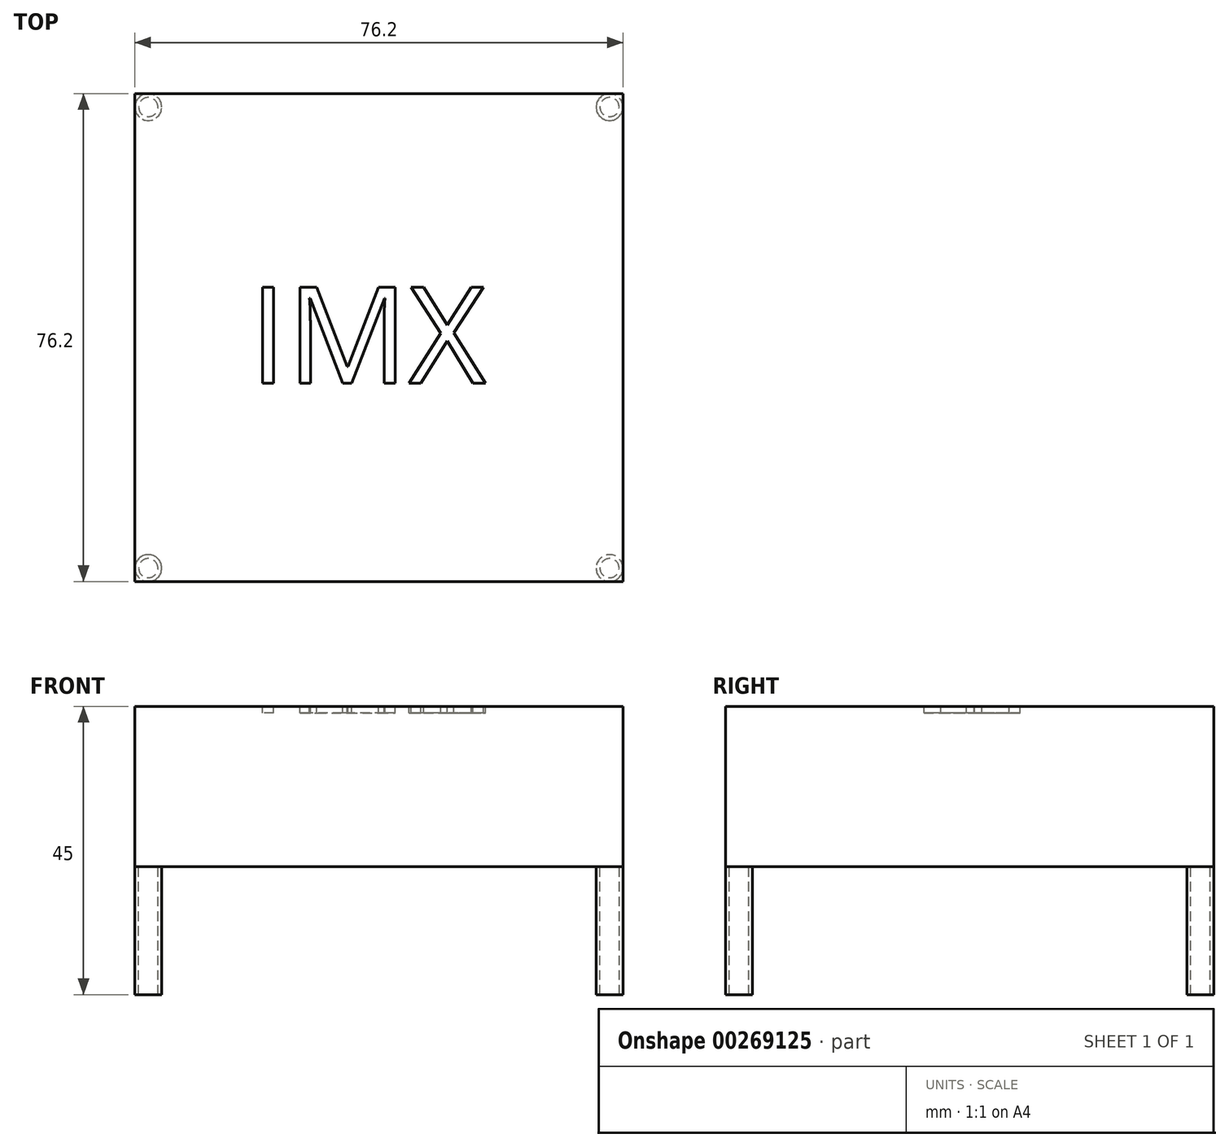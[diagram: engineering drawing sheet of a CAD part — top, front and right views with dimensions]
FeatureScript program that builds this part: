
annotation { "Feature Type Name" : "Feature", "Feature Type Description" : "" }
export const myFeature = defineFeature(function(context is Context, id is Id, definition is map)
    precondition{}
    {
        {
            var Q0;
            Q0=qCreatedBy(makeId("Top.planeOp"),FACE);
            var sketch = newSketch(context, id + "F0", { "sketchPlane" : qUnion([Q0])});
            skLineSegment(sketch, "E0.bottom", {"start": v(38.1, 38.1) * mm, "end": v(-38.1, 38.1) * mm});
            skLineSegment(sketch, "E0.top", {"start": v(38.1, -38.1) * mm, "end": v(-38.1, -38.1) * mm});
            skLineSegment(sketch, "E0.left", {"start": v(38.1, 38.1) * mm, "end": v(38.1, -38.1) * mm});
            skLineSegment(sketch, "E0.right", {"start": v(-38.1, 38.1) * mm, "end": v(-38.1, -38.1) * mm});
            skPoint(sketch, "E0.middle", {"position": v(0, 0) * mm});
            skSolve(sketch);
        }
        {
            var Q0;
            Q0 = qSketchRegion(id + "F0", true);
            extrude(context, id + "F1", {"entities" : qUnion([Q0]), "depth" : 25 * mm});
        }
        {
            var Q0;
            Q0=makeQuery(id+"F1.opExtrude","CAP_FACE",FACE,{"disambiguationData":[OSD([sQuery(id+"F0.wireOp",EDGE,"E0.bottom"),sQuery(id+"F0.wireOp",EDGE,"E0.top"),sQuery(id+"F0.wireOp",EDGE,"E0.left"),sQuery(id+"F0.wireOp",EDGE,"E0.right")])],"isStart":true});
            var sketch = newSketch(context, id + "F2", { "sketchPlane" : qUnion([Q0])});
            skCircle(sketch, "E1", {"center": v(-36, 36) * mm, "radius": 2.1 * mm});
            skCircle(sketch, "E2", {"center": v(36, 36) * mm, "radius": 2.1 * mm});
            skCircle(sketch, "E3", {"center": v(-36, -36) * mm, "radius": 2.1 * mm});
            skCircle(sketch, "E4", {"center": v(36, -36) * mm, "radius": 2.1 * mm});
            skCircle(sketch, "E5", {"center": v(-36, 36) * mm, "radius": 1.5 * mm});
            skCircle(sketch, "E6", {"center": v(36, 36) * mm, "radius": 1.5 * mm});
            skCircle(sketch, "E7", {"center": v(36, -36) * mm, "radius": 1.5 * mm});
            skCircle(sketch, "E8", {"center": v(-36, -36) * mm, "radius": 1.5 * mm});
            skSolve(sketch);
        }
        {
            var Q0;
            Q0 = qSketchRegion(id + "F2", true);
            extrude(context, id + "F3", {"entities" : qUnion([Q0]), "operationType" : NewBodyOperationType.ADD, "depth" : 20 * mm});
        }
        {
            var Q0;
            Q0=makeQuery(id+"F1.opExtrude","CAP_FACE",FACE,{"disambiguationData":[OSD([sQuery(id+"F0.wireOp",EDGE,"E0.bottom"),sQuery(id+"F0.wireOp",EDGE,"E0.top"),sQuery(id+"F0.wireOp",EDGE,"E0.left"),sQuery(id+"F0.wireOp",EDGE,"E0.right")])],"isStart":false});
            var sketch = newSketch(context, id + "F4", { "sketchPlane" : qUnion([Q0])});
            skText(sketch, "E9", { "text": "IMX", "fontName": "OpenSans-Regular.ttf"});
            const initialGuessF4  = {"E9": [-0.02024, -0.00713, 1, 0, 0.01514]};
            skSetInitialGuess(sketch, initialGuessF4);
            skSolve(sketch);
        }
        {
            var Q0;
            Q0 = qSketchRegion(id + "F4", true);
            extrude(context, id + "F5", {"entities" : qUnion([Q0]), "operationType" : NewBodyOperationType.REMOVE, "oppositeDirection" : true, "depth" : 1 * mm});
        }
    });
